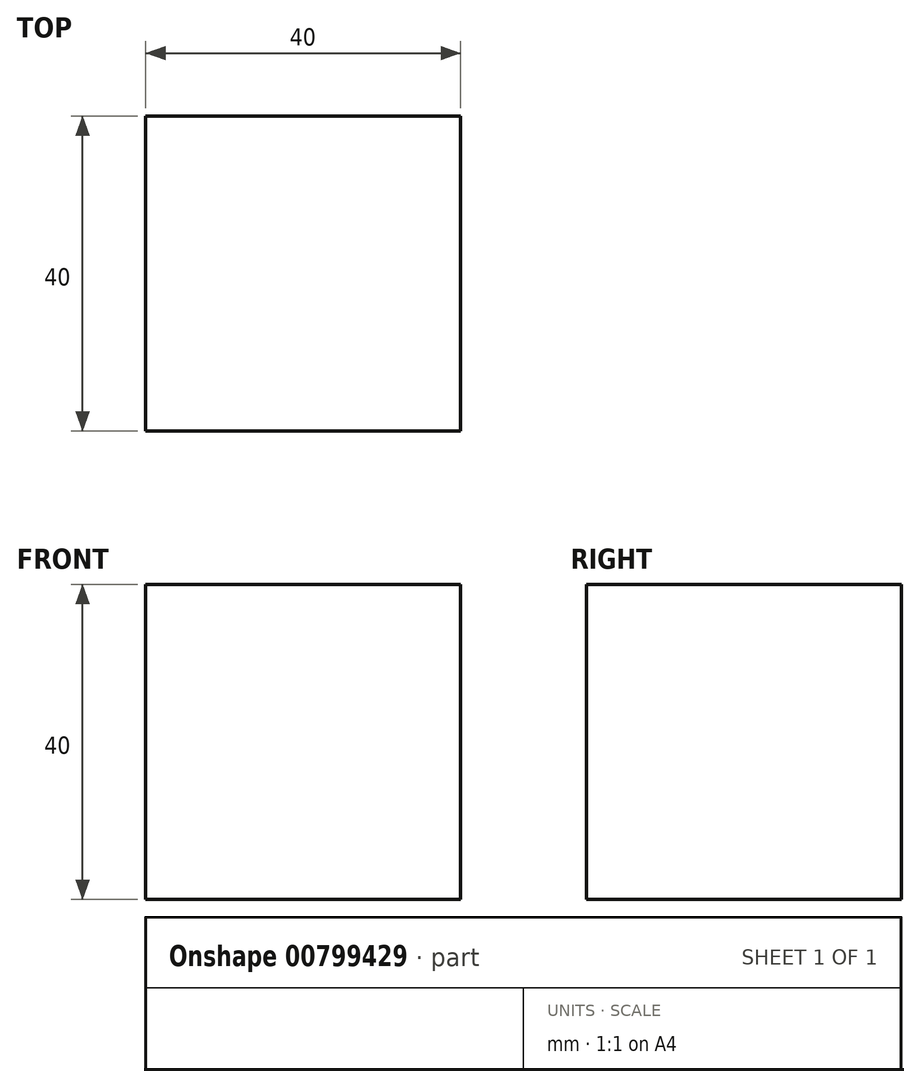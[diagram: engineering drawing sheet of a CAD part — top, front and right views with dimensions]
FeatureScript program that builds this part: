
annotation { "Feature Type Name" : "Feature", "Feature Type Description" : "" }
export const myFeature = defineFeature(function(context is Context, id is Id, definition is map)
    precondition{}
    {
        {
            var Q0;
            Q0=qCreatedBy(makeId("Top.planeOp"),FACE);
            var sketch = newSketch(context, id + "F0", { "sketchPlane" : qUnion([Q0])});
            skLineSegment(sketch, "E0.bottom", {"start": v(0, 0) * mm, "end": v(40, 0) * mm});
            skLineSegment(sketch, "E0.top", {"start": v(0, 40) * mm, "end": v(40, 40) * mm});
            skLineSegment(sketch, "E0.left", {"start": v(0, 0) * mm, "end": v(0, 40) * mm});
            skLineSegment(sketch, "E0.right", {"start": v(40, 0) * mm, "end": v(40, 40) * mm});
            skSolve(sketch);
        }
        {
            var Q0;
            Q0 = qSketchRegion(id + "F0", true);
            extrude(context, id + "F1", {"entities" : qUnion([Q0]), "depth" : 40 * mm, "offsetDistance" : 25 * mm});
        }
    });
